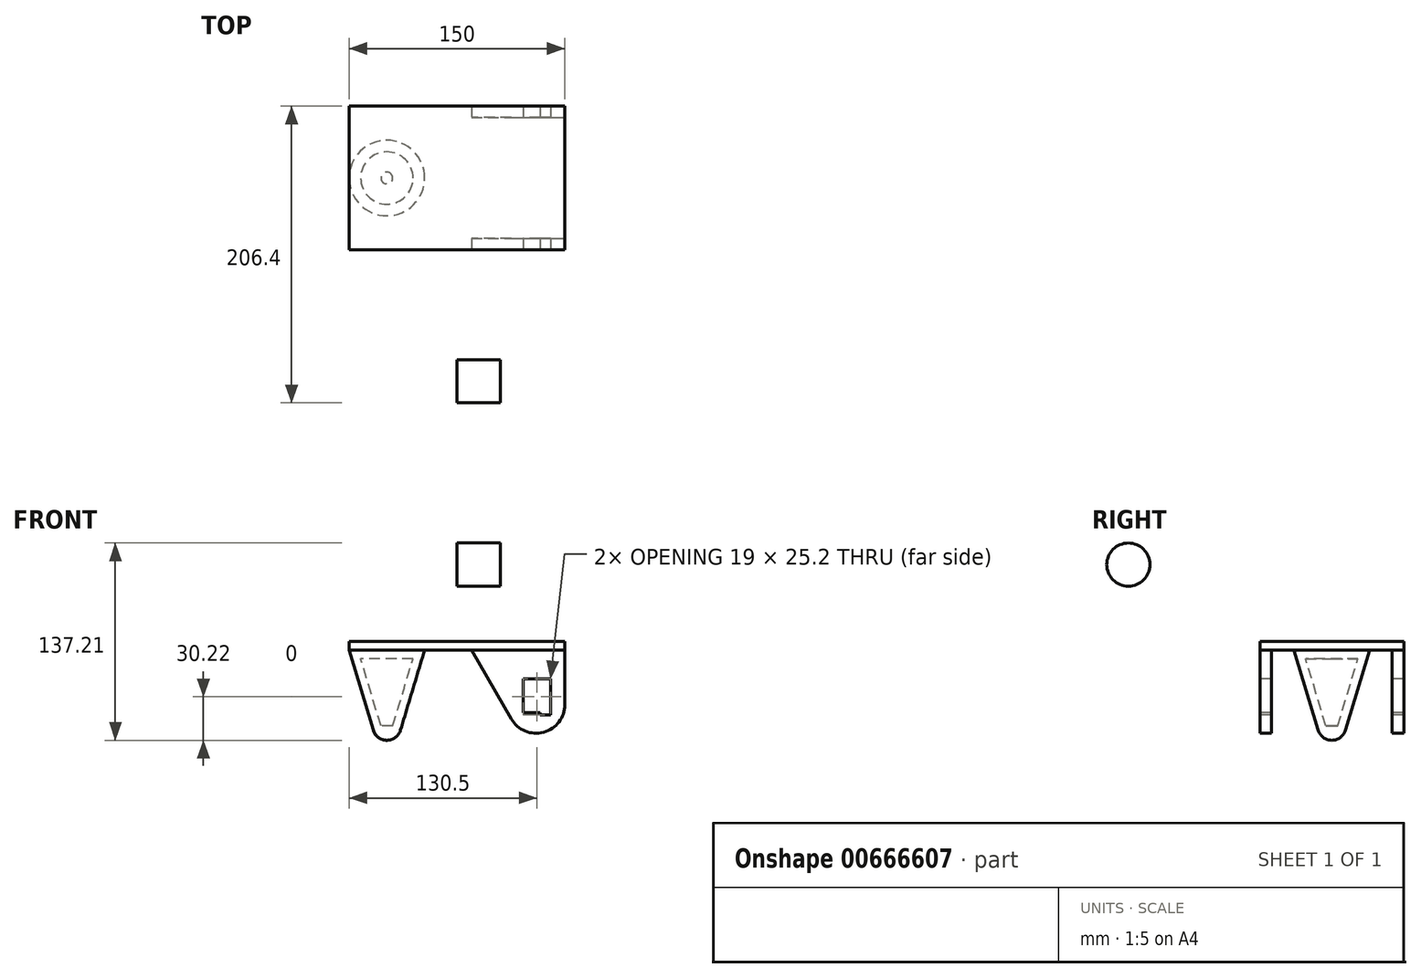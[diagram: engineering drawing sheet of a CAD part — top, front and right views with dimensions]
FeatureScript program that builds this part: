
annotation { "Feature Type Name" : "Feature", "Feature Type Description" : "" }
export const myFeature = defineFeature(function(context is Context, id is Id, definition is map)
    precondition{}
    {
        {
            var Q0;
            Q0=qCreatedBy(makeId("Top.planeOp"),FACE);
            var sketch = newSketch(context, id + "F0", { "sketchPlane" : qUnion([Q0])});
            skLineSegment(sketch, "E0.bottom", {"start": v(-75, 50) * mm, "end": v(75, 50) * mm});
            skLineSegment(sketch, "E0.top", {"start": v(-75, -50) * mm, "end": v(75, -50) * mm});
            skLineSegment(sketch, "E0.left", {"start": v(-75, 50) * mm, "end": v(-75, -50) * mm});
            skLineSegment(sketch, "E0.right", {"start": v(75, 50) * mm, "end": v(75, -50) * mm});
            skPoint(sketch, "E0.middle", {"position": v(0, 0) * mm});
            skSolve(sketch);
        }
        {
            var Q0;
            Q0=makeQuery(id+"F0.imprint","IMPRINT",FACE,{"disambiguationData":[TD([[makeQuery(id+"F0.imprint","IMPRINT",EDGE,{"derivedFrom":sQuery(id+"F0.wireOp",EDGE,"E0.bottom")}),-1.0]])]});
            extrude(context, id + "F1", {"entities" : qUnion([Q0]), "depth" : 6 * mm, "offsetDistance" : 25.4 * mm});
        }
        {
            var Q0;
            Q0=makeQuery(id+"F1.opExtrude","SWEPT_FACE",FACE,{"disambiguationData":[OSD([sQuery(id+"F0.wireOp",EDGE,"E0.top")])]});
            var sketch = newSketch(context, id + "F2", { "sketchPlane" : qUnion([Q0])});
            skLineSegment(sketch, "E1", {"start": v(65, -20) * mm, "end": v(46, -20) * mm});
            skLineSegment(sketch, "E2", {"start": v(10, 0) * mm, "end": v(75, 0) * mm});
            skLineSegment(sketch, "E3", {"start": v(75, 0) * mm, "end": v(75, -37.94) * mm});
            skLineSegment(sketch, "E4", {"start": v(10, 0) * mm, "end": v(37.68, -47.94) * mm});
            skArc(sketch, "E5.filletArc", {"start": v(37.68, -47.94) * mm, "mid": v(60.18, -57.26) * mm, "end": v(75, -37.94) * mm});
            skLineSegment(sketch, "E6.MirrorCS", {"start": v(57.8, -43.7) * mm, "end": v(57.8, -45.2) * mm});
            skLineSegment(sketch, "E7.MirrorCS", {"start": v(46, -43.7) * mm, "end": v(57.8, -43.7) * mm});
            skLineSegment(sketch, "E8.MirrorCS", {"start": v(46, -43.7) * mm, "end": v(46, -20) * mm});
            skLineSegment(sketch, "E9.MirrorCS", {"start": v(65, -45.2) * mm, "end": v(65, -20) * mm});
            skLineSegment(sketch, "E10.MirrorCS", {"start": v(57.8, -45.2) * mm, "end": v(65, -45.2) * mm});
            skSolve(sketch);
        }
        {
            var Q0;
            Q0=qCreatedBy(makeId("Top.planeOp"),FACE);
            var sketch = newSketch(context, id + "F3", { "sketchPlane" : qUnion([Q0])});
            skLineSegment(sketch, "E11.bottom", {"start": v(-60.46, 42) * mm, "end": v(110.6, 42) * mm});
            skLineSegment(sketch, "E11.top", {"start": v(-60.46, -42) * mm, "end": v(110.6, -42) * mm});
            skLineSegment(sketch, "E11.left", {"start": v(-60.46, 42) * mm, "end": v(-60.46, -42) * mm});
            skLineSegment(sketch, "E11.right", {"start": v(110.6, 42) * mm, "end": v(110.6, -42) * mm});
            skSolve(sketch);
        }
        {
            var Q0;
            Q0=qCreatedBy(makeId("Front.planeOp"),FACE);
            var sketch = newSketch(context, id + "F4", { "sketchPlane" : qUnion([Q0])});
            skLineSegment(sketch, "E12", {"start": v(-75, 0) * mm, "end": v(-48.74, 0) * mm});
            skLineSegment(sketch, "E13", {"start": v(-48.74, 0) * mm, "end": v(-48.74, -87.3) * mm});
            skLineSegment(sketch, "E14", {"start": v(-48.74, -87.3) * mm, "end": v(-75, 0) * mm});
            skCircle(sketch, "E15", {"center": v(-48.74, -52.92) * mm, "radius": 9.9 * mm});
            skLineSegment(sketch, "E16", {"start": v(-48.74, -6) * mm, "end": v(-66.93, -6) * mm});
            skLineSegment(sketch, "E17", {"start": v(-66.93, -6) * mm, "end": v(-52.82, -52.92) * mm});
            skLineSegment(sketch, "E18", {"start": v(-52.82, -52.92) * mm, "end": v(-48.74, -52.92) * mm});
            skLineSegment(sketch, "E19", {"start": v(-48.74, -62.82) * mm, "end": v(75.33, -62.82) * mm});
            skCircle(sketch, "E20", {"center": v(55.77, -39.7) * mm, "radius": 23.12 * mm});
            skSolve(sketch);
        }
        {
            var Q0;
            Q0=makeQuery(id+"F2.imprint","IMPRINT",FACE,{"disambiguationData":[TD([[makeQuery(id+"F2.imprint","IMPRINT",EDGE,{"derivedFrom":sQuery(id+"F2.wireOp",EDGE,"E1")}),-1.0]])]});
            extrude(context, id + "F5", {"entities" : qUnion([Q0]), "oppositeDirection" : true, "depth" : 100 * mm, "offsetDistance" : 25 * mm});
        }
        {
            var Q0;
            Q0=makeQuery(id+"F3.imprint","IMPRINT",FACE,{"disambiguationData":[TD([[makeQuery(id+"F3.imprint","IMPRINT",EDGE,{"derivedFrom":sQuery(id+"F3.wireOp",EDGE,"E11.bottom")}),-1.0]])]});
            extrude(context, id + "F6", {"entities" : qUnion([Q0]), "operationType" : NewBodyOperationType.REMOVE, "oppositeDirection" : true, "depth" : 200 * mm, "offsetDistance" : 25 * mm});
        }
        {
            var Q0;
            {var subQ5=sQuery(id+"F4.wireOp",EDGE,"E12");Q0=makeQuery(id+"F4.imprint","IMPRINT",FACE,{"disambiguationData":[TD([[makeQuery(id+"F4.imprint","IMPRINT",EDGE,{"derivedFrom":subQ5}),-1.0]])]});}
            var Q1;
            {var subQ4=sQuery(id+"F4.wireOp",EDGE,"E18");Q1=makeQuery(id+"F4.imprint","IMPRINT",FACE,{"disambiguationData":[TD([[makeQuery(id+"F4.imprint","IMPRINT",EDGE,{"derivedFrom":subQ4}),-1.0]])]});}
            var Q2;
            Q2=sQuery(id+"F4.wireOp",EDGE,"E13");
            revolve(context, id + "F7", {"operationType" : NewBodyOperationType.ADD, "entities" : qUnion([Q0, Q1]), "axis" : qUnion([Q2]), "revolveType" : RevolveType.FULL});
        }
        {
            var Q0;
            Q0=qCreatedBy(makeId("Right.planeOp"),FACE);
            var sketch = newSketch(context, id + "F8", { "sketchPlane" : qUnion([Q0])});
            skCircle(sketch, "E21", {"center": v(-141.4, 59.4) * mm, "radius": 15 * mm});
            skSolve(sketch);
        }
        {
            var Q0;
            Q0 = qSketchRegion(id + "F8", true);
            extrude(context, id + "F9", {"entities" : qUnion([Q0]), "depth" : 30 * mm, "offsetDistance" : 25 * mm});
        }
    });
